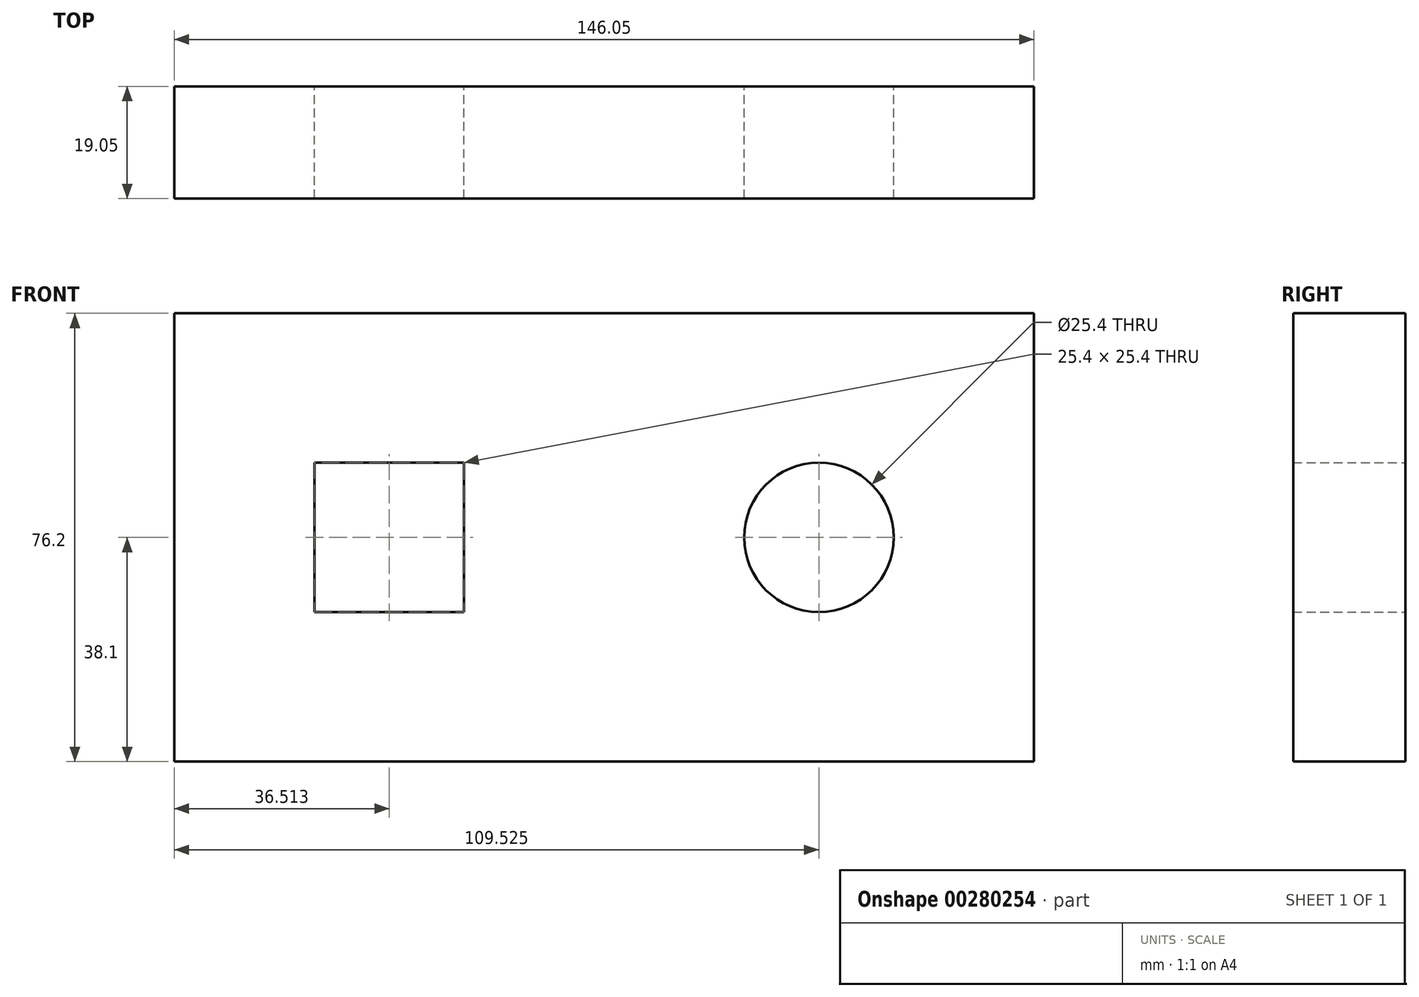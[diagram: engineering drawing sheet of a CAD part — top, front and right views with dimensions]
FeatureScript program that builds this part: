
annotation { "Feature Type Name" : "Feature", "Feature Type Description" : "" }
export const myFeature = defineFeature(function(context is Context, id is Id, definition is map)
    precondition{}
    {
        {
            var Q0;
            Q0=qCreatedBy(makeId("Front.planeOp"),FACE);
            var sketch = newSketch(context, id + "F0", { "sketchPlane" : qUnion([Q0])});
            skLineSegment(sketch, "E0.bottom", {"start": v(0, 0) * mm, "end": v(-146.05, 0) * mm});
            skLineSegment(sketch, "E0.top", {"start": v(0, 76.2) * mm, "end": v(-146.05, 76.2) * mm});
            skLineSegment(sketch, "E0.left", {"start": v(0, 0) * mm, "end": v(0, 76.2) * mm});
            skLineSegment(sketch, "E0.right", {"start": v(-146.05, 0) * mm, "end": v(-146.05, 76.2) * mm});
            skCircle(sketch, "E1", {"center": v(-36.53, 38.1) * mm, "radius": 12.7 * mm});
            skLineSegment(sketch, "E2.bottom", {"start": v(-122.24, 50.8) * mm, "end": v(-96.84, 50.8) * mm});
            skLineSegment(sketch, "E2.top", {"start": v(-122.24, 25.4) * mm, "end": v(-96.84, 25.4) * mm});
            skLineSegment(sketch, "E2.left", {"start": v(-122.24, 50.8) * mm, "end": v(-122.24, 25.4) * mm});
            skLineSegment(sketch, "E2.right", {"start": v(-96.84, 50.8) * mm, "end": v(-96.84, 25.4) * mm});
            skSolve(sketch);
        }
        {
            var Q0;
            Q0 = qSketchRegion(id + "F0", true);
            extrude(context, id + "F1", {"entities" : qUnion([Q0]), "depth" : 19.05 * mm});
        }
    });
